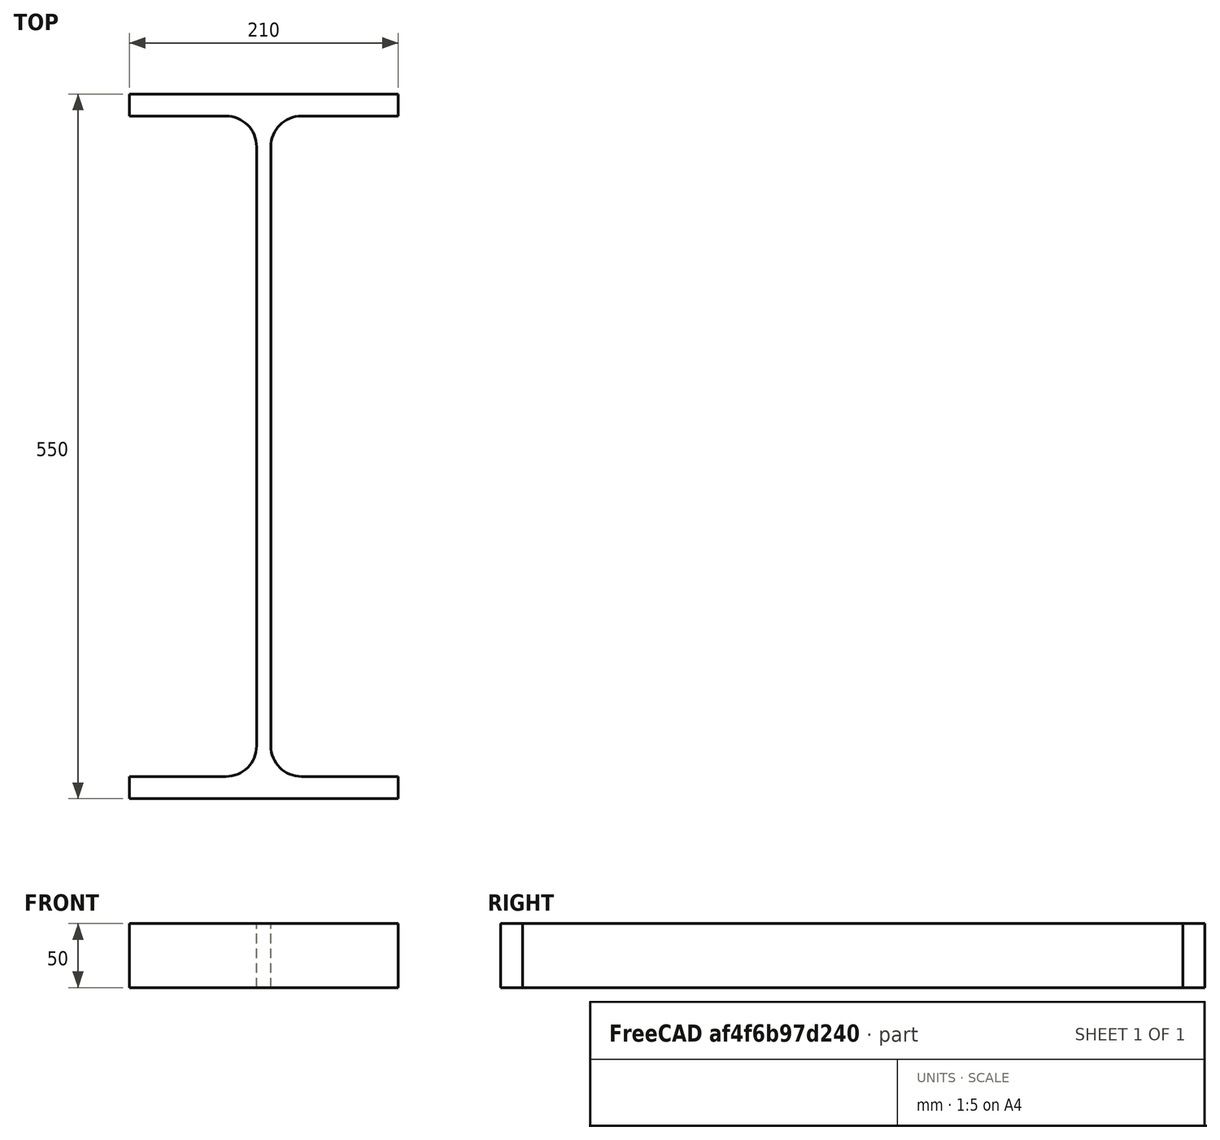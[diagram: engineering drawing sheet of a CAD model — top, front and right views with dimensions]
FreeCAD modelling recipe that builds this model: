
FCSTD DOCUMENT  (FreeCAD 0.15R4671 (Git))
Label: IPE-Profile 550 DIN1025-5 S235JR
License: All rights reserved
LicenseURL: http://en.wikipedia.org/wiki/All_rights_reserved
objects: Sketcher::SketchObject×1, Part::Extrusion×1
note: 2 computed .brp shape members not serialized (recipe doc carries the construction recipe); baked Part::Feature solids carry a one-line shape summary decoded from their .brp

FEATURE [Sketcher::SketchObject] Sketch
  sketch-geometry (16):
    g0: LineSegment StartX=5.55 StartY=-233.8 StartZ=0 EndX=5.55 EndY=233.8 EndZ=0
    g1: LineSegment StartX=29.55 StartY=257.8 StartZ=0 EndX=105 EndY=257.8 EndZ=0
    g2: LineSegment StartX=105 StartY=257.8 StartZ=0 EndX=105 EndY=275 EndZ=0
    g3: LineSegment StartX=105 StartY=275 StartZ=0 EndX=-105 EndY=275 EndZ=0
    g4: LineSegment StartX=-105 StartY=275 StartZ=0 EndX=-105 EndY=257.8 EndZ=0
    g5: LineSegment StartX=-105 StartY=257.8 StartZ=0 EndX=-29.55 EndY=257.8 EndZ=0
    g6: LineSegment StartX=-5.55 StartY=233.8 StartZ=0 EndX=-5.55 EndY=-233.8 EndZ=0
    g7: LineSegment StartX=-29.55 StartY=-257.8 StartZ=0 EndX=-105 EndY=-257.8 EndZ=0
    g8: LineSegment StartX=-105 StartY=-257.8 StartZ=0 EndX=-105 EndY=-275 EndZ=0
    g9: LineSegment StartX=-105 StartY=-275 StartZ=0 EndX=105 EndY=-275 EndZ=0
    g10: LineSegment StartX=105 StartY=-275 StartZ=0 EndX=105 EndY=-257.8 EndZ=0
    g11: LineSegment StartX=105 StartY=-257.8 StartZ=0 EndX=29.55 EndY=-257.8 EndZ=0
    g12: ArcOfCircle CenterX=29.55 CenterY=233.8 CenterZ=0 NormalX=0 NormalY=0 NormalZ=1 Radius=24 StartAngle=1.5708 EndAngle=3.14159
    g13: ArcOfCircle CenterX=29.55 CenterY=-233.8 CenterZ=0 NormalX=0 NormalY=0 NormalZ=1 Radius=24 StartAngle=3.14159 EndAngle=4.71239
    g14: ArcOfCircle CenterX=-29.55 CenterY=233.8 CenterZ=0 NormalX=0 NormalY=0 NormalZ=1 Radius=24 StartAngle=0 EndAngle=1.5708
    g15: ArcOfCircle CenterX=-29.55 CenterY=-233.8 CenterZ=0 NormalX=0 NormalY=0 NormalZ=1 Radius=24 StartAngle=4.71239 EndAngle=6.28319
  constraints (42):
    c: Vertical(g0)
    c: Coincident(g2,g1)
    c: Vertical(g2)
    c: Coincident(g3,g2)
    c: Coincident(g4,g3)
    c: Vertical(g4)
    c: Coincident(g5,g4)
    c: Horizontal(g5)
    c: Vertical(g6)
    c: Horizontal(g7)
    c: Coincident(g8,g7)
    c: Vertical(g8)
    c: Coincident(g9,g8)
    c: Horizontal(g9)
    c: Coincident(g10,g9)
    c: Vertical(g10)
    c: Coincident(g11,g10)
    c: Horizontal(g11)
    c: Tangent(g1,g12) = 1.5708
    c: Tangent(g0,g12) = 1.5708
    c: Tangent(g0,g13) = 1.5708
    c: Tangent(g11,g13) = 1.5708
    c: Tangent(g5,g14) = 1.5708
    c: Tangent(g6,g14) = 1.5708
    c: Tangent(g6,g15) = 1.5708
    c: Tangent(g7,g15) = 1.5708
    c: Equal(g3,g9)
    c: Equal(g2,g4)
    c: Equal(g4,g8)
    c: Equal(g8,g10)
    c: Equal(g12,g14)
    c: Equal(g14,g15)
    c: Equal(g15,g13)
    c: Symmetric(g2,g3,g-2)
    c: Symmetric(g9,g8,g-2)
    c: Symmetric(g0,g6,g-2)
    c: Symmetric(g2,g9,g-1)
    c: DistanceY(g2,g9) = -550
    c: DistanceX(g3) = -210
    c: DistanceX(g0,g6) = -11.1
    c: DistanceY(g2) = 17.2
    c: Radius(g12) = 24
FEATURE [Part::Extrusion] Extrude  label="IPE-Profile 550 DIN1025-5 S235JR"
  Base = -> Sketch
  Dir = (0,0,50)
  Solid = true
